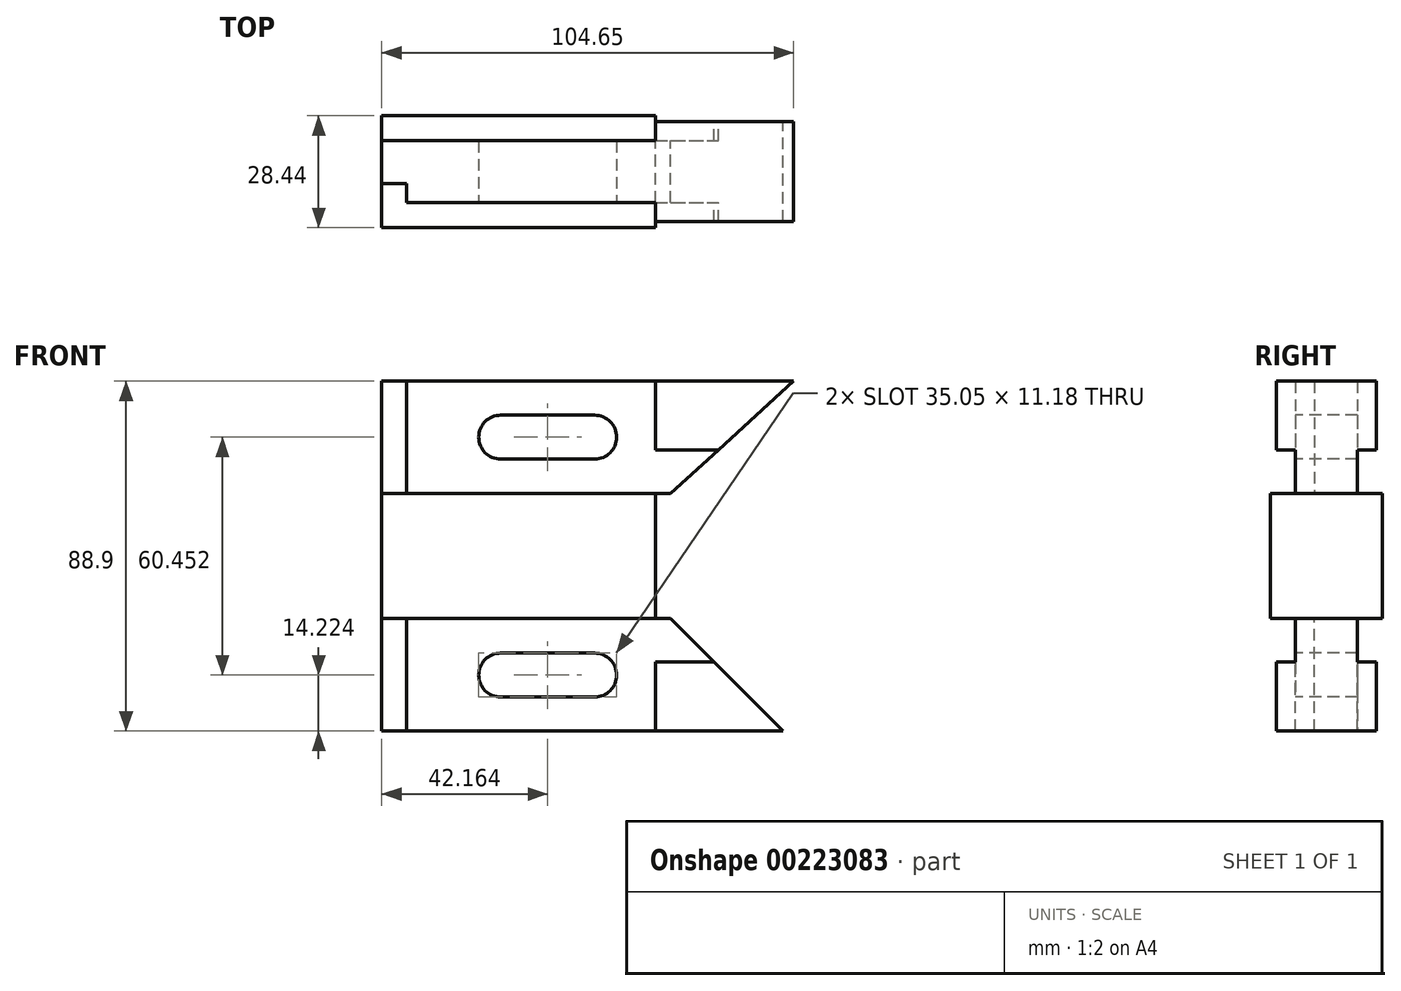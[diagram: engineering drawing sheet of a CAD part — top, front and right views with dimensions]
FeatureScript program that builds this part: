
annotation { "Feature Type Name" : "Feature", "Feature Type Description" : "" }
export const myFeature = defineFeature(function(context is Context, id is Id, definition is map)
    precondition{}
    {
        {
            var Q0;
            Q0=qCreatedBy(makeId("Front.planeOp"),FACE);
            var sketch = newSketch(context, id + "F0", { "sketchPlane" : qUnion([Q0])});
            skLineSegment(sketch, "E0", {"start": v(0, 0) * mm, "end": v(0, -88.9) * mm});
            skLineSegment(sketch, "E1", {"start": v(0, 0) * mm, "end": v(104.65, 0) * mm});
            skLineSegment(sketch, "E2", {"start": v(0, 0) * mm, "end": v(0, -44.45) * mm});
            skLineSegment(sketch, "E3", {"start": v(0, 0) * mm, "end": v(0, -28.58) * mm, "construction": true});
            skLineSegment(sketch, "E4", {"start": v(0, -28.58) * mm, "end": v(73.4, -28.58) * mm});
            skLineSegment(sketch, "E5", {"start": v(73.4, -28.58) * mm, "end": v(104.65, 0) * mm});
            skLineSegment(sketch, "E6", {"start": v(0, 0) * mm, "end": v(6.35, 0) * mm, "construction": true});
            skLineSegment(sketch, "E7", {"start": v(6.35, 0) * mm, "end": v(6.35, -28.58) * mm});
            skLineSegment(sketch, "E8", {"start": v(0, 0) * mm, "end": v(6.35, 0) * mm});
            skLineSegment(sketch, "E9", {"start": v(69.6, 0) * mm, "end": v(69.6, -17.53) * mm});
            skLineSegment(sketch, "E10", {"start": v(69.6, -17.53) * mm, "end": v(85.49, -17.53) * mm});
            skPoint(sketch, "E11.endSnap0", {"position": v(0, -14.29) * mm});
            skLineSegment(sketch, "E12", {"start": v(0, -28.58) * mm, "end": v(0, -60.32) * mm});
            skLineSegment(sketch, "E13", {"start": v(0, -60.32) * mm, "end": v(69.6, -60.32) * mm});
            skLineSegment(sketch, "E14", {"start": v(69.6, -60.32) * mm, "end": v(69.6, -28.57) * mm});
            skLineSegment(sketch, "E15.MirrorCS", {"start": v(0, -88.9) * mm, "end": v(101.98, -88.9) * mm});
            skLineSegment(sketch, "E16.MirrorCS", {"start": v(73.4, -60.32) * mm, "end": v(101.98, -88.9) * mm});
            skLineSegment(sketch, "E17.MirrorCS", {"start": v(69.6, -88.9) * mm, "end": v(69.6, -71.37) * mm});
            skLineSegment(sketch, "E18.MirrorCS", {"start": v(69.6, -71.37) * mm, "end": v(84.46, -71.37) * mm});
            skLineSegment(sketch, "E19.MirrorCS", {"start": v(6.35, -88.9) * mm, "end": v(6.35, -60.32) * mm});
            skPoint(sketch, "E11.start.orphan", {"position": v(0, -14.29) * mm});
            skLineSegment(sketch, "E20", {"start": v(69.6, -60.32) * mm, "end": v(73.4, -60.32) * mm});
            skLineSegment(sketch, "E21", {"start": v(73.4, -28.58) * mm, "end": v(69.6, -28.57) * mm, "construction": true});
            skLineSegment(sketch, "E22", {"start": v(0, -60.32) * mm, "end": v(6.35, -60.32) * mm, "construction": true});
            skSolve(sketch);
        }
        {
            var Q0;
            {var subQ7=sQuery(id+"F0.wireOp",EDGE,"E14");Q0=makeQuery(id+"F0.imprint","IMPRINT",FACE,{"disambiguationData":[TD([[makeQuery(id+"F0.imprint","IMPRINT",EDGE,{"derivedFrom":subQ7}),1.0]])]});}
            extrude(context, id + "F1", {"entities" : qUnion([Q0]), "endBound" : BoundingType.SYMMETRIC, "depth" : 28.45 * mm});
        }
        {
            var Q0;
            {var subQ0=sQuery(id+"F0.wireOp",EDGE,"E17.MirrorCS");Q0=makeQuery(id+"F0.imprint","IMPRINT",FACE,{"disambiguationData":[TD([[makeQuery(id+"F0.imprint","IMPRINT",EDGE,{"derivedFrom":subQ0}),1.0]])]});}
            var Q1;
            {var subQ5=sQuery(id+"F0.wireOp",EDGE,"E7");Q1=makeQuery(id+"F0.imprint","IMPRINT",FACE,{"disambiguationData":[TD([[makeQuery(id+"F0.imprint","IMPRINT",EDGE,{"derivedFrom":subQ5}),1.0]])]});}
            extrude(context, id + "F2", {"entities" : qUnion([Q0, Q1]), "operationType" : NewBodyOperationType.ADD, "endBound" : BoundingType.SYMMETRIC, "depth" : 15.75 * mm});
        }
        {
            var Q0;
            {var subQ3=sQuery(id+"F0.wireOp",EDGE,"E9");Q0=makeQuery(id+"F0.imprint","IMPRINT",FACE,{"disambiguationData":[TD([[makeQuery(id+"F0.imprint","IMPRINT",EDGE,{"derivedFrom":subQ3}),1.0]])]});}
            var Q1;
            {var subQ3=sQuery(id+"F0.wireOp",EDGE,"E17.MirrorCS");Q1=makeQuery(id+"F0.imprint","IMPRINT",FACE,{"disambiguationData":[TD([[makeQuery(id+"F0.imprint","IMPRINT",EDGE,{"derivedFrom":subQ3}),-1.0]])]});}
            extrude(context, id + "F3", {"entities" : qUnion([Q0, Q1]), "operationType" : NewBodyOperationType.ADD, "endBound" : BoundingType.SYMMETRIC, "depth" : 25.4 * mm});
        }
        {
            var Q0;
            {var subQ0=sQuery(id+"F0.wireOp",EDGE,"E2");Q0=makeQuery(id+"F0.imprint","IMPRINT",FACE,{"disambiguationData":[TD([[makeQuery(id+"F0.imprint","IMPRINT",EDGE,{"derivedFrom":subQ0}),1.0]])]});}
            var Q1;
            {var subQ0=sQuery(id+"F0.wireOp",EDGE,"E0");Q1=makeQuery(id+"F0.imprint","IMPRINT",FACE,{"disambiguationData":[TD([[makeQuery(id+"F0.imprint","IMPRINT",EDGE,{"derivedFrom":subQ0}),1.0]])]});}
            extrude(context, id + "F4", {"entities" : qUnion([Q0, Q1]), "operationType" : NewBodyOperationType.ADD, "endBound" : BoundingType.SYMMETRIC, "depth" : 15.75 * mm});
        }
        {
            var Q0;
            {var subQ0=sQuery(id+"F0.wireOp",EDGE,"E7");var subQ1=sQuery(id+"F0.wireOp",EDGE,"E4");Q0=makeQuery(id+"F4.boolean.opBoolean","MERGE",FACE,{"derivedFrom":[makeQuery(id+"F2.opExtrude","CAP_FACE",FACE,{"disambiguationData":[OSD([sQuery(id+"F0.wireOp",EDGE,"E1"),subQ1,sQuery(id+"F0.wireOp",EDGE,"E5"),subQ0,sQuery(id+"F0.wireOp",EDGE,"E9"),sQuery(id+"F0.wireOp",EDGE,"E10")])],"isStart":false}),makeQuery(id+"F4.opExtrude","CAP_FACE",FACE,{"disambiguationData":[OSD([sQuery(id+"F0.wireOp",EDGE,"E2"),subQ1,subQ0,sQuery(id+"F0.wireOp",EDGE,"E8")])],"isStart":false})]});}
            var sketch = newSketch(context, id + "F5", { "sketchPlane" : qUnion([Q0])});
            skLineSegment(sketch, "E23.0", {"start": v(6.35, 0) * mm, "end": v(6.35, -28.58) * mm});
            skLineSegment(sketch, "E24.0", {"start": v(0, 0) * mm, "end": v(0, -28.58) * mm});
            skLineSegment(sketch, "E25.0", {"start": v(0, -28.58) * mm, "end": v(6.35, -28.58) * mm});
            skLineSegment(sketch, "E26.0", {"start": v(0, 0) * mm, "end": v(6.35, 0) * mm});
            skPoint(sketch, "E27.orphan", {"position": v(0, -44.45) * mm});
            skPoint(sketch, "E28.orphan", {"position": v(73.4, -28.58) * mm});
            skPoint(sketch, "E29.orphan", {"position": v(69.6, 0) * mm});
            skLineSegment(sketch, "E30", {"start": v(0, -44.45) * mm, "end": v(18.82, -44.45) * mm, "construction": true});
            skLineSegment(sketch, "E31.MirrorCS", {"start": v(0, -88.9) * mm, "end": v(0, -60.33) * mm});
            skLineSegment(sketch, "E32.MirrorCS", {"start": v(0, -60.33) * mm, "end": v(6.35, -60.33) * mm});
            skLineSegment(sketch, "E33.MirrorCS", {"start": v(6.35, -88.9) * mm, "end": v(6.35, -60.32) * mm});
            skLineSegment(sketch, "E34.MirrorCS", {"start": v(0, -88.9) * mm, "end": v(6.35, -88.9) * mm});
            skSolve(sketch);
        }
        {
            var Q0;
            Q0 = qSketchRegion(id + "F5", true);
            extrude(context, id + "F6", {"entities" : qUnion([Q0]), "operationType" : NewBodyOperationType.REMOVE, "oppositeDirection" : true, "depth" : 4.83 * mm});
        }
        {
            var Q0;
            {var subQ0=sQuery(id+"F0.wireOp",EDGE,"E7");var subQ1=sQuery(id+"F0.wireOp",EDGE,"E4");Q0=makeQuery(id+"F4.boolean.opBoolean","MERGE",FACE,{"derivedFrom":[makeQuery(id+"F2.opExtrude","CAP_FACE",FACE,{"disambiguationData":[OSD([sQuery(id+"F0.wireOp",EDGE,"E1"),subQ1,sQuery(id+"F0.wireOp",EDGE,"E5"),subQ0,sQuery(id+"F0.wireOp",EDGE,"E9"),sQuery(id+"F0.wireOp",EDGE,"E10")])],"isStart":false}),makeQuery(id+"F4.opExtrude","CAP_FACE",FACE,{"disambiguationData":[OSD([sQuery(id+"F0.wireOp",EDGE,"E2"),subQ1,subQ0,sQuery(id+"F0.wireOp",EDGE,"E8")])],"isStart":false})]});}
            var sketch = newSketch(context, id + "F7", { "sketchPlane" : qUnion([Q0])});
            skLineSegment(sketch, "E35.0", {"start": v(0, 0) * mm, "end": v(0, -44.45) * mm, "construction": true});
            skPoint(sketch, "E36.0", {"position": v(34.8, -28.58) * mm});
            skLineSegment(sketch, "E37.0", {"start": v(0, -28.58) * mm, "end": v(69.6, -28.58) * mm, "construction": true});
            skLineSegment(sketch, "E38", {"start": v(69.6, -28.58) * mm, "end": v(69.6, 0) * mm, "construction": true});
            skLineSegment(sketch, "E39", {"start": v(69.6, 0) * mm, "end": v(0, 0) * mm, "construction": true});
            skArc(sketch, "E40", {"start": v(30.23, -8.64) * mm, "mid": v(24.64, -14.22) * mm, "end": v(30.23, -19.81) * mm});
            skArc(sketch, "E41", {"start": v(54.1, -19.81) * mm, "mid": v(59.69, -14.22) * mm, "end": v(54.1, -8.64) * mm});
            skLineSegment(sketch, "E42", {"start": v(30.23, -14.22) * mm, "end": v(24.64, -14.22) * mm, "construction": true});
            skLineSegment(sketch, "E43", {"start": v(30.23, -14.22) * mm, "end": v(54.1, -14.22) * mm, "construction": true});
            skLineSegment(sketch, "E44", {"start": v(54.1, -14.22) * mm, "end": v(59.69, -14.22) * mm, "construction": true});
            skLineSegment(sketch, "E45", {"start": v(30.23, -19.81) * mm, "end": v(54.1, -19.81) * mm});
            skLineSegment(sketch, "E46", {"start": v(30.23, -8.64) * mm, "end": v(54.1, -8.64) * mm});
            skLineSegment(sketch, "E47", {"start": v(0, -44.45) * mm, "end": v(16.73, -44.45) * mm, "construction": true});
            skLineSegment(sketch, "E48.MirrorCS", {"start": v(30.23, -80.26) * mm, "end": v(54.1, -80.26) * mm});
            skArc(sketch, "E49.MirrorCS", {"start": v(54.1, -69.09) * mm, "mid": v(59.69, -74.68) * mm, "end": v(54.1, -80.26) * mm});
            skArc(sketch, "E50.MirrorCS", {"start": v(30.23, -80.26) * mm, "mid": v(24.64, -74.68) * mm, "end": v(30.23, -69.09) * mm});
            skLineSegment(sketch, "E51.MirrorCS", {"start": v(30.23, -74.68) * mm, "end": v(54.1, -74.68) * mm, "construction": true});
            skLineSegment(sketch, "E52.MirrorCS", {"start": v(54.1, -74.68) * mm, "end": v(59.69, -74.68) * mm, "construction": true});
            skLineSegment(sketch, "E53.MirrorCS", {"start": v(30.23, -69.09) * mm, "end": v(54.1, -69.09) * mm});
            skLineSegment(sketch, "E54.MirrorCS", {"start": v(30.23, -74.68) * mm, "end": v(24.64, -74.68) * mm, "construction": true});
            skSolve(sketch);
        }
        {
            var Q0;
            Q0 = qSketchRegion(id + "F7", true);
            extrude(context, id + "F8", {"entities" : qUnion([Q0]), "operationType" : NewBodyOperationType.REMOVE, "endBound" : BoundingType.THROUGH_ALL, "oppositeDirection" : true, "depth" : 25.4 * mm});
        }
    });
